# Revit family: XL H
name_source: partatom
category: Generic Models
units: mm (PartAtom-declared; Revit-internal decimal feet)

## family parameters
Can host rebar = No
Cut with Voids When Loaded = No
Host = Face
Maintain Annotation Orientation = No
Part Type = Normal
Room Calculation Point = No
Round Connector Dimension = Use Diameter
Shared = No

## types (1)
- XL H
    Angle Stairsupporuts = 150.00°
    Ceiling height = 3500 mm
    Closed = Yes
    Closing angle hatch = 90.00°
    Cradle mat. = Multiplex
    Default Elevation = 1219 mm
    Depth cradle = 1490 mm  [stored 4.88845 ft]
    Moving angle inner stinger = 144.00°
    Open = No
    Railing Left = Yes
    Railing Right = Yes
    Stair face controle = 300 mm
    Stairhinge lock = 287 mm  [stored 0.941601 ft]
    Stinger mat. = Aluminium
    Voidcontrole top = 55 mm  [stored 0.180446 ft]
    Wheels mat. = Poly
    Width cradle = 987 mm  [stored 3.23819 ft]
    Width supports = 600 mm

note: [stored X ft] marks values corroborated as IEEE doubles in the binary element streams (Revit-internal decimal feet)

## geometry (parser evidence)
native form markers: Sweep x53
no freeform markers — native parametric forms only
